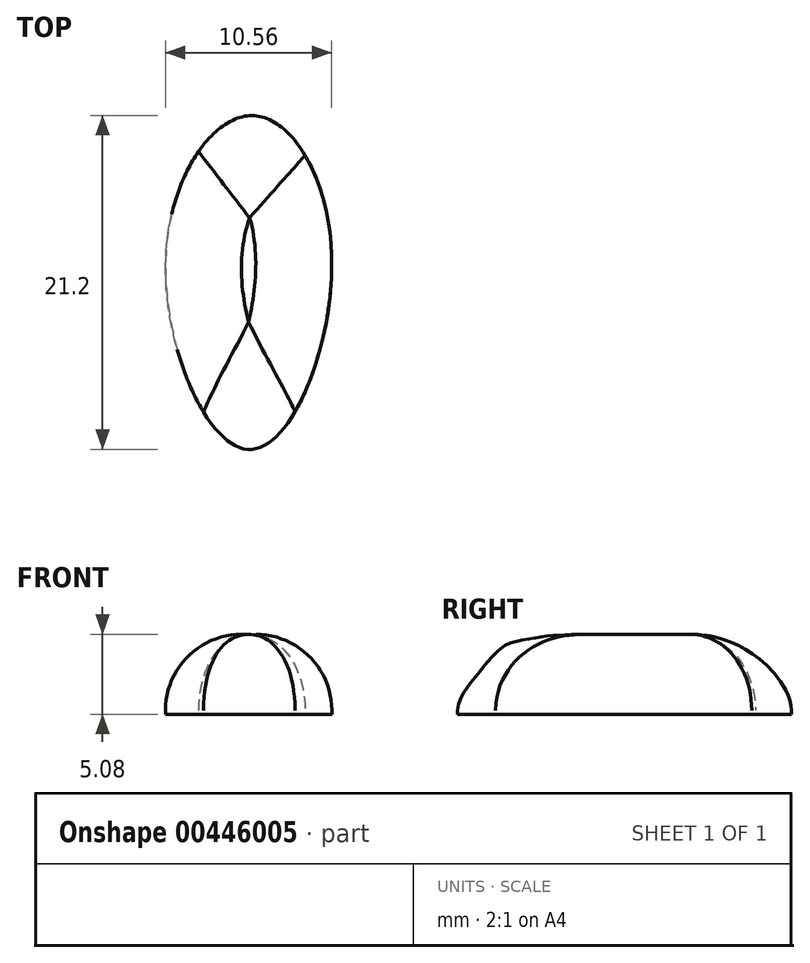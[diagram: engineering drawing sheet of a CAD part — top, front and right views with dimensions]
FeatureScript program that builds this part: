
annotation { "Feature Type Name" : "Feature", "Feature Type Description" : "" }
export const myFeature = defineFeature(function(context is Context, id is Id, definition is map)
    precondition{}
    {
        {
            var Q0;
            Q0=qCreatedBy(makeId("Top.planeOp"),FACE);
            var sketch = newSketch(context, id + "F0", { "sketchPlane" : qUnion([Q0])});
            skFitSpline(sketch, "E0", {"points": [v(-6.6, 10.15) * mm, v(-12.08, 1.3) * mm, v(-6.75, -11.05) * mm, v(-1.55, 1.44) * mm, v(-6.6, 10.15) * mm]});
            skSolve(sketch);
        }
        {
            var Q0;
            Q0 = qSketchRegion(id + "F0", true);
            extrude(context, id + "F1", {"entities" : qUnion([Q0]), "depth" : 5.08 * mm});
        }
        {
            var Q0;
            Q0=makeQuery(id+"F1.opExtrude","CAP_FACE",FACE,{"disambiguationData":[OSD([sQuery(id+"F0.wireOp",EDGE,"E0")])],"isStart":false});
            fillet(context, id + "F2", {"entities" : qUnion([Q0]), "radius" : 4.83 * mm, "tangentPropagation" : true, "allowEdgeOverflow" : false});
        }
    });
